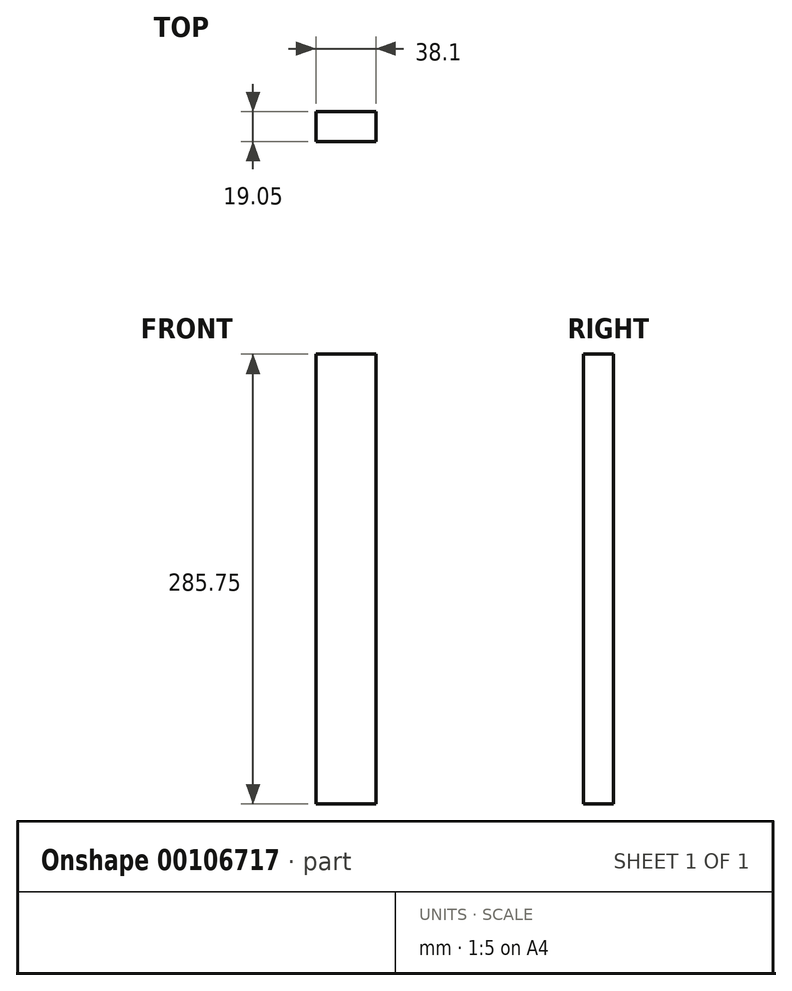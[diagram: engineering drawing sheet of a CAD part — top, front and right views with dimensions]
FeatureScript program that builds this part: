
annotation { "Feature Type Name" : "Feature", "Feature Type Description" : "" }
export const myFeature = defineFeature(function(context is Context, id is Id, definition is map)
    precondition{}
    {
        {
            var Q0;
            Q0=qCreatedBy(makeId("Front.planeOp"),FACE);
            var sketch = newSketch(context, id + "F0", { "sketchPlane" : qUnion([Q0])});
            skLineSegment(sketch, "E0.bottom", {"start": v(0, 0) * mm, "end": v(38.1, 0) * mm});
            skLineSegment(sketch, "E0.top", {"start": v(0, 285.75) * mm, "end": v(38.1, 285.75) * mm});
            skLineSegment(sketch, "E0.left", {"start": v(0, 0) * mm, "end": v(0, 285.75) * mm});
            skLineSegment(sketch, "E0.right", {"start": v(38.1, 0) * mm, "end": v(38.1, 285.75) * mm});
            skSolve(sketch);
        }
        {
            var Q0;
            Q0=makeQuery(id+"F0.imprint","IMPRINT",FACE,{"disambiguationData":[TD([[makeQuery(id+"F0.imprint","IMPRINT",EDGE,{"derivedFrom":sQuery(id+"F0.wireOp",EDGE,"E0.bottom")}),1.0]])]});
            extrude(context, id + "F1", {"entities" : qUnion([Q0]), "depth" : 19.05 * mm});
        }
    });
